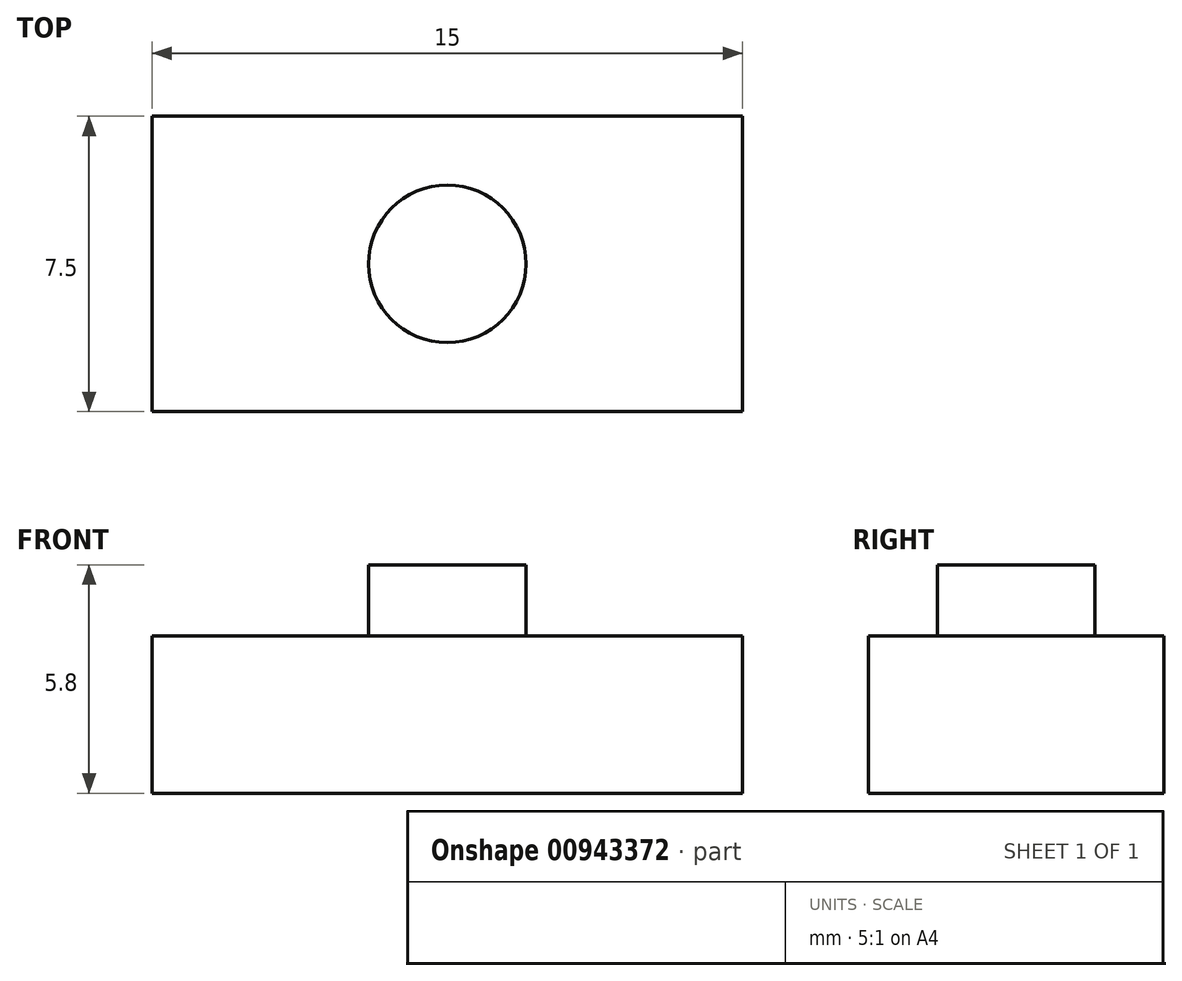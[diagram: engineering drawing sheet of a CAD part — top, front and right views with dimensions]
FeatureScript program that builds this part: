
annotation { "Feature Type Name" : "Feature", "Feature Type Description" : "" }
export const myFeature = defineFeature(function(context is Context, id is Id, definition is map)
    precondition{}
    {
        {
            var Q0;
            Q0=qCreatedBy(makeId("Top.planeOp"),FACE);
            var sketch = newSketch(context, id + "F0", { "sketchPlane" : qUnion([Q0])});
            skLineSegment(sketch, "E0.bottom", {"start": v(-7.5, -3.75) * mm, "end": v(7.5, -3.75) * mm});
            skLineSegment(sketch, "E0.top", {"start": v(-7.5, 3.75) * mm, "end": v(7.5, 3.75) * mm});
            skLineSegment(sketch, "E0.left", {"start": v(-7.5, -3.75) * mm, "end": v(-7.5, 3.75) * mm});
            skLineSegment(sketch, "E0.right", {"start": v(7.5, -3.75) * mm, "end": v(7.5, 3.75) * mm});
            skPoint(sketch, "E0.middle", {"position": v(0, 0) * mm});
            skSolve(sketch);
        }
        {
            var Q0;
            Q0 = qSketchRegion(id + "F0", true);
            extrude(context, id + "F1", {"entities" : qUnion([Q0]), "depth" : 4 * mm, "offsetDistance" : 25 * mm});
        }
        {
            var Q0;
            Q0=makeQuery(id+"F1.opExtrude","CAP_FACE",FACE,{"disambiguationData":[OSD([sQuery(id+"F0.wireOp",EDGE,"E0.bottom"),sQuery(id+"F0.wireOp",EDGE,"E0.top"),sQuery(id+"F0.wireOp",EDGE,"E0.left"),sQuery(id+"F0.wireOp",EDGE,"E0.right")])],"isStart":false});
            var sketch = newSketch(context, id + "F2", { "sketchPlane" : qUnion([Q0])});
            skCircle(sketch, "E1", {"center": v(0, 0) * mm, "radius": 2 * mm});
            skSolve(sketch);
        }
        {
            var Q0;
            Q0=makeQuery(id+"F2.imprint","IMPRINT",FACE,{"disambiguationData":[TD([[makeQuery(id+"F2.imprint","IMPRINT",EDGE,{"derivedFrom":sQuery(id+"F2.wireOp",EDGE,"E1")}),1.0]])]});
            extrude(context, id + "F3", {"entities" : qUnion([Q0]), "operationType" : NewBodyOperationType.ADD, "depth" : 1.8 * mm, "offsetDistance" : 25 * mm});
        }
    });
